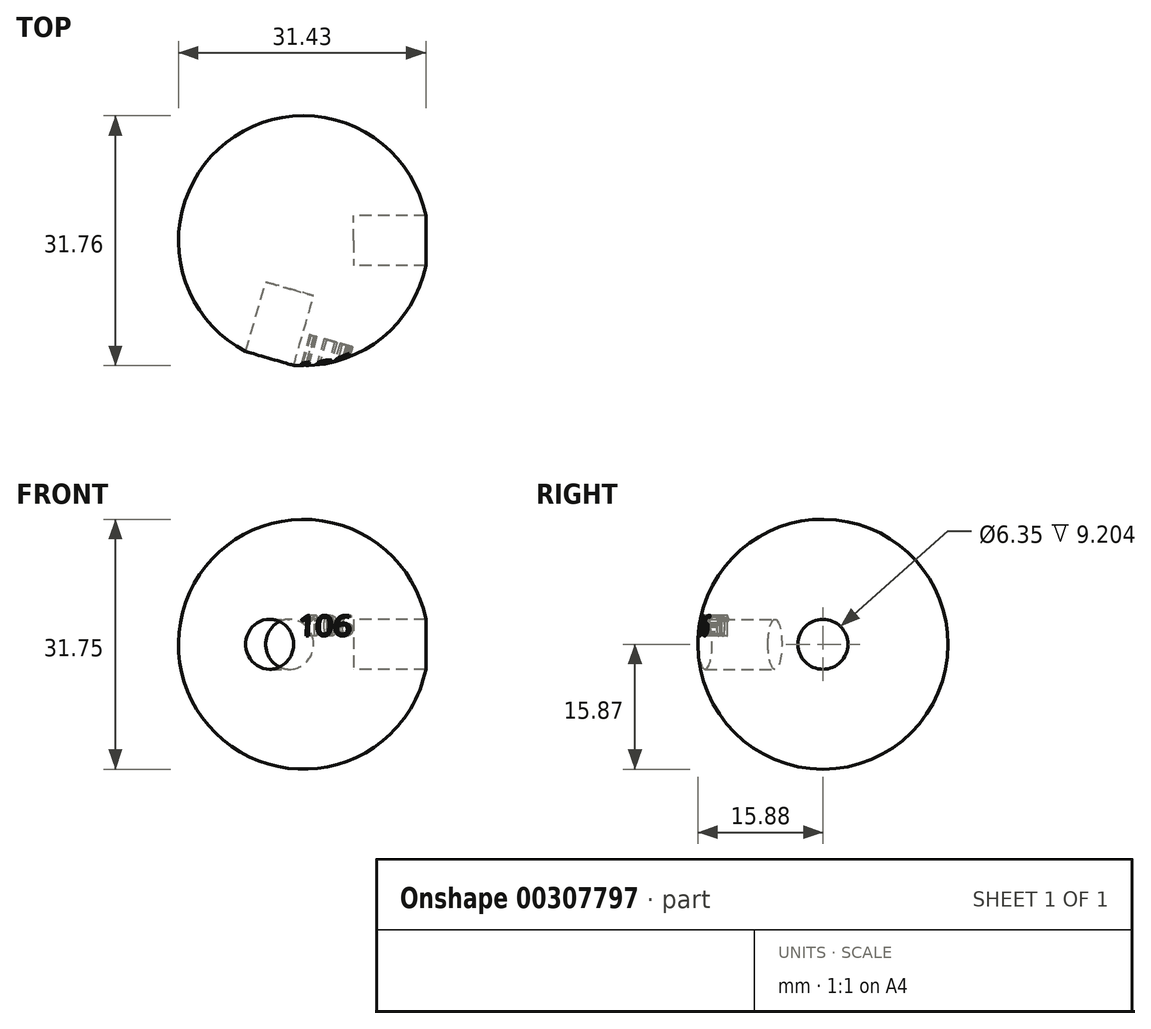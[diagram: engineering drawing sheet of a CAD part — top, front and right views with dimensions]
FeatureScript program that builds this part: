
annotation { "Feature Type Name" : "Feature", "Feature Type Description" : "" }
export const myFeature = defineFeature(function(context is Context, id is Id, definition is map)
    precondition{}
    {
        {
            var Q0;
            Q0=qCreatedBy(makeId("Top.planeOp"),FACE);
            var sketch = newSketch(context, id + "F0", { "sketchPlane" : qUnion([Q0])});
            skArc(sketch, "E0", {"start": v(0, 15.88) * mm, "mid": v(-15.88, 0) * mm, "end": v(0, -15.88) * mm});
            skLineSegment(sketch, "E1", {"start": v(0, 15.88) * mm, "end": v(0, -15.88) * mm});
            skSolve(sketch);
        }
        {
            var Q0;
            Q0=makeQuery(id+"F0.imprint","IMPRINT",FACE,{"disambiguationData":[TD([[makeQuery(id+"F0.imprint","IMPRINT",EDGE,{"derivedFrom":sQuery(id+"F0.wireOp",EDGE,"E0")}),1.0]])]});
            var Q1;
            Q1=sQuery(id+"F0.wireOp",EDGE,"E1");
            revolve(context, id + "F1", {"entities" : qUnion([Q0]), "axis" : qUnion([Q1]), "revolveType" : RevolveType.FULL});
        }
        {
            var Q0;
            Q0=qCreatedBy(makeId("Top.planeOp"),FACE);
            var sketch = newSketch(context, id + "F2", { "sketchPlane" : qUnion([Q0])});
            skLineSegment(sketch, "E2", {"start": v(0, 0) * mm, "end": v(0, -56.41) * mm, "construction": true});
            skLineSegment(sketch, "E3", {"start": v(0, 0) * mm, "end": v(75.03, 0) * mm, "construction": true});
            skSolve(sketch);
        }
        {
            var Q0;
            Q0=qCreatedBy(makeId("Top.planeOp"),FACE);
            cPlane(context, id + "F3", {"entities" : qUnion([Q0]), "cplaneType" : CPlaneType.OFFSET, "offset" : 6.35 * mm, "width" : 152.4 * mm, "height" : 152.4 * mm});
        }
        {
            var Q0;
            Q0=qCreatedBy(id+"F3.planeOp",FACE);
            var sketch = newSketch(context, id + "F4", { "sketchPlane" : qUnion([Q0])});
            skCircle(sketch, "E4", {"center": v(0, 0) * mm, "radius": 3.18 * mm});
            skSolve(sketch);
        }
        {
            var Q0;
            Q0 = qSketchRegion(id + "F4", true);
            extrude(context, id + "F5", {"entities" : qUnion([Q0]), "depth" : 25.4 * mm});
        }
        {
            var Q0;
            Q0=makeQuery(id+"F5.opExtrude","SWEPT_BODY",BODY,{"disambiguationData":[OSD([sQuery(id+"F4.wireOp",EDGE,"E4")])]});
            var Q1;
            Q1=sQuery(id+"F2.wireOp",EDGE,"E3");
            var Q2;
            Q2=sQuery(id+"F2.wireOp",EDGE,"E3");
            transform(context, id + "F6", {"entities" : qUnion([Q0]), "transformType" : TransformType.ROTATION, "transformAxis" : qUnion([Q2]), "angle" : 106 * degree, "makeCopy" : true});
        }
        {
            var Q0;
            Q0=makeQuery(id+"F6.opPattern","COPY",BODY,{"derivedFrom":makeQuery(id+"F5.opExtrude","SWEPT_BODY",BODY,{"disambiguationData":[OSD([sQuery(id+"F4.wireOp",EDGE,"E4")])]}),"instanceName":"1"});
            var Q1;
            Q1=makeQuery(id+"F5.opExtrude","SWEPT_BODY",BODY,{"disambiguationData":[OSD([sQuery(id+"F4.wireOp",EDGE,"E4")])]});
            var Q2;
            Q2=makeQuery(id+"F1.opRevolve","SWEPT_BODY",BODY,{"disambiguationData":[OSD([sQuery(id+"F0.wireOp",EDGE,"E0"),sQuery(id+"F0.wireOp",EDGE,"E1")])]});
            booleanBodies(context, id + "F7", {"operationType" : BooleanOperationType.SUBTRACTION, "tools" : qUnion([Q0, Q1]), "targets" : qUnion([Q2])});
        }
        {
            var Q0;
            Q0=makeQuery(id+"F1.opRevolve","SWEPT_BODY",BODY,{"disambiguationData":[OSD([sQuery(id+"F0.wireOp",EDGE,"E0"),sQuery(id+"F0.wireOp",EDGE,"E1")])]});
            var Q1;
            Q1=sQuery(id+"F2.wireOp",EDGE,"E2");
            transform(context, id + "F8", {"entities" : qUnion([Q0]), "transformType" : TransformType.ROTATION, "transformAxis" : qUnion([Q1]), "angle" : 90 * degree, "oppositeDirection" : true, "makeCopy" : false});
        }
        {
            var Q0;
            Q0=makeQuery(id+"F7.opBoolean","COPY",FACE,{"derivedFrom":makeQuery(id+"F6.opPattern","COPY",FACE,{"derivedFrom":makeQuery(id+"F5.opExtrude","CAP_FACE",FACE,{"disambiguationData":[OSD([sQuery(id+"F4.wireOp",EDGE,"E4")])],"isStart":true}),"instanceName":"1"})});
            cPlane(context, id + "F9", {"entities" : qUnion([Q0]), "cplaneType" : CPlaneType.OFFSET, "offset" : 15.54 * mm, "width" : 152.4 * mm, "height" : 152.4 * mm});
        }
        {
            var Q0;
            Q0=qCreatedBy(id+"F9.planeOp",FACE);
            var sketch = newSketch(context, id + "F10", { "sketchPlane" : qUnion([Q0])});
            skText(sketch, "E5", { "text": "106", "fontName": "OpenSans-Regular.ttf"});
            const initialGuessF10  = {"E5": [0.00372, 0.00108, 1, 0, 0.00259]};
            skSetInitialGuess(sketch, initialGuessF10);
            skSolve(sketch);
        }
        {
            var Q0;
            Q0 = qSketchRegion(id + "F10", true);
            extrude(context, id + "F11", {"entities" : qUnion([Q0]), "operationType" : NewBodyOperationType.REMOVE, "oppositeDirection" : true, "depth" : 10.64 * mm});
        }
    });
